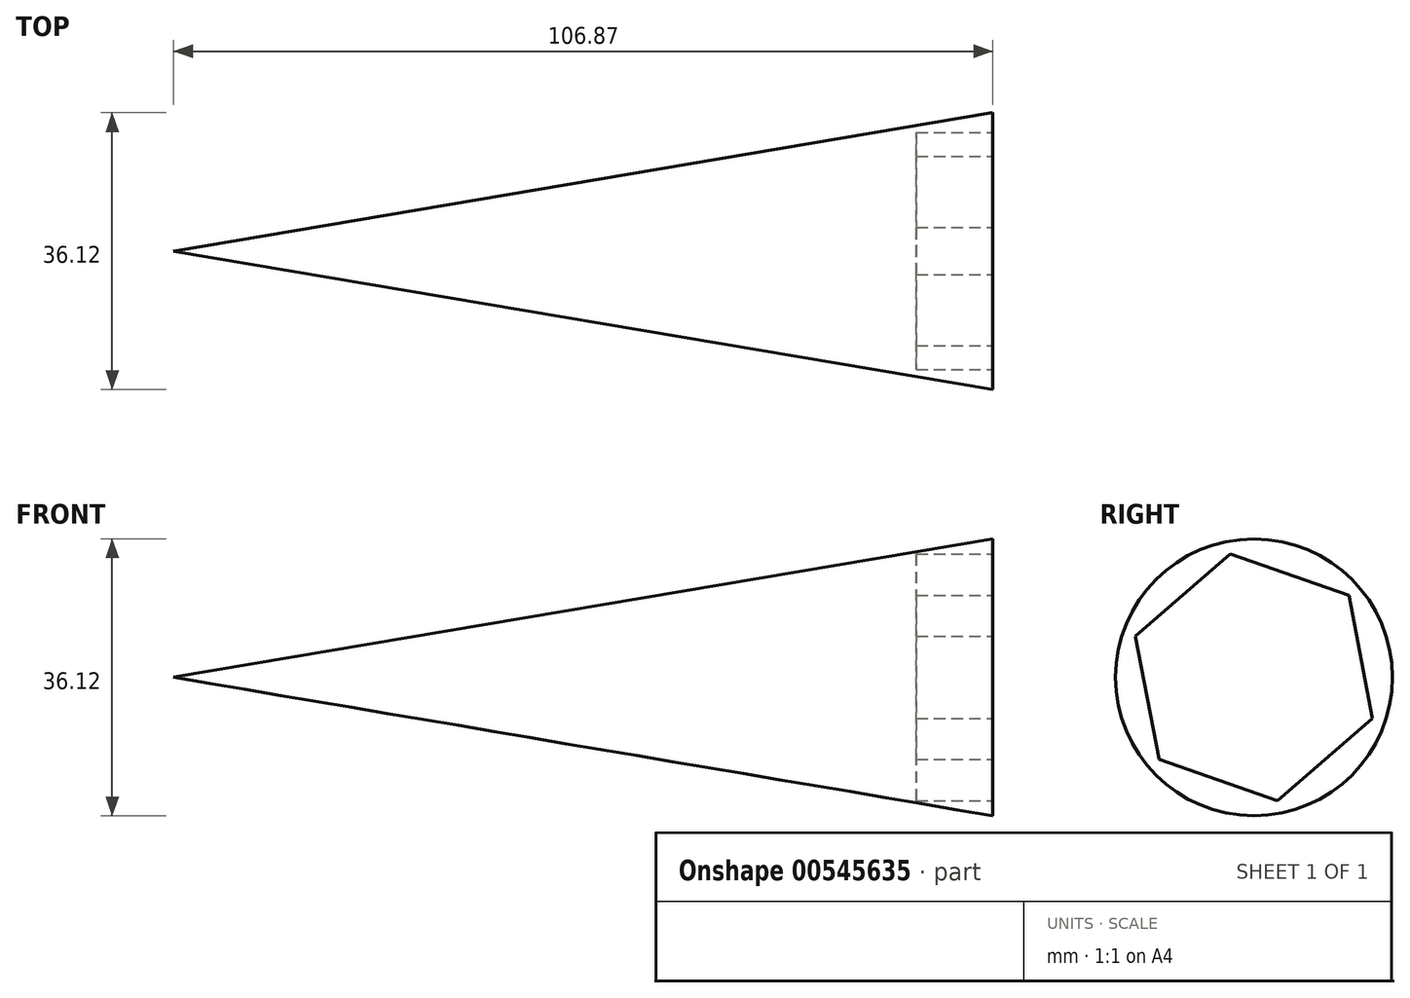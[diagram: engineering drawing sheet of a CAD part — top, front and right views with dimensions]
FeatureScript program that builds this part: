
annotation { "Feature Type Name" : "Feature", "Feature Type Description" : "" }
export const myFeature = defineFeature(function(context is Context, id is Id, definition is map)
    precondition{}
    {
        {
            var Q0;
            Q0=qCreatedBy(makeId("Front.planeOp"),FACE);
            var sketch = newSketch(context, id + "F0", { "sketchPlane" : qUnion([Q0])});
            skLineSegment(sketch, "E0", {"start": v(-47.96, 0) * mm, "end": v(58.91, 0) * mm});
            skLineSegment(sketch, "E1", {"start": v(58.91, 0) * mm, "end": v(58.91, 18.06) * mm});
            skLineSegment(sketch, "E2", {"start": v(-47.96, 0) * mm, "end": v(58.91, 18.06) * mm});
            skSolve(sketch);
        }
        {
            var Q0;
            Q0=makeQuery(id+"F0.imprint","IMPRINT",FACE,{"disambiguationData":[TD([[makeQuery(id+"F0.imprint","IMPRINT",EDGE,{"derivedFrom":sQuery(id+"F0.wireOp",EDGE,"E0")}),1.0]])]});
            var Q1;
            Q1=sQuery(id+"F0.wireOp",EDGE,"E0");
            revolve(context, id + "F1", {"entities" : qUnion([Q0]), "axis" : qUnion([Q1]), "revolveType" : RevolveType.FULL});
        }
        {
            var Q0;
            Q0=makeQuery(id+"F1.opRevolve","SWEPT_FACE",FACE,{"disambiguationData":[OSD([sQuery(id+"F0.wireOp",EDGE,"E1")])]});
            var sketch = newSketch(context, id + "F2", { "sketchPlane" : qUnion([Q0])});
            skCircle(sketch, "E3.cCircle", {"center": v(0, 0) * mm, "radius": 14.17 * mm, "construction": true});
            skLineSegment(sketch, "E3.0", {"start": v(12.38, 10.7) * mm, "end": v(15.45, -5.37) * mm});
            skLineSegment(sketch, "E3.1", {"start": v(15.45, -5.37) * mm, "end": v(3.08, -16.07) * mm});
            skLineSegment(sketch, "E3.2", {"start": v(3.08, -16.07) * mm, "end": v(-12.38, -10.7) * mm});
            skLineSegment(sketch, "E3.3", {"start": v(-12.38, -10.7) * mm, "end": v(-15.45, 5.37) * mm});
            skLineSegment(sketch, "E3.4", {"start": v(-15.45, 5.37) * mm, "end": v(-3.08, 16.07) * mm});
            skLineSegment(sketch, "E3.5", {"start": v(-3.08, 16.07) * mm, "end": v(12.38, 10.7) * mm});
            skPoint(sketch, "E3.0.midPoint", {"position": v(13.91, 2.66) * mm});
            skSolve(sketch);
        }
        {
            var Q0;
            Q0=makeQuery(id+"F2.imprint","IMPRINT",FACE,{"disambiguationData":[TD([[makeQuery(id+"F2.imprint","IMPRINT",EDGE,{"derivedFrom":sQuery(id+"F2.wireOp",EDGE,"E3.0")}),-1.0]])]});
            extrude(context, id + "F3", {"entities" : qUnion([Q0]), "operationType" : NewBodyOperationType.REMOVE, "oppositeDirection" : true, "depth" : 10 * mm, "offsetDistance" : 25 * mm});
        }
    });
